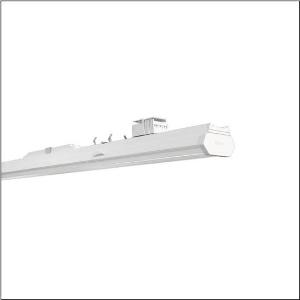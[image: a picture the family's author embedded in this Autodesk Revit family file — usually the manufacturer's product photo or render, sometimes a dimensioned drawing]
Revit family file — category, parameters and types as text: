
# Revit family: licross_r__11_protected_mo_51td12dn495g3c_9d50
name_source: partatom
category: Lighting Fixtures
units: mm (PartAtom-declared; Revit-internal decimal feet)

## family parameters
Cut with Voids When Loaded = No
Host = Face
Light Source = No
Part Type = Normal
Room Calculation Point = No
Round Connector Dimension = Use Diameter
Shared = No

## types (1)
- --- (1 x LED, 980 lm, 6.8 W, 4000K)
    Apparent Load = 7 VA
    CIE Flux Codes = 73 92 98 99 100
    Color Rendering = 80
    Color Temperature = 4000K
    Default Elevation = 1800 mm
    Description = Licross® 11 Protected MO, luminaire insert, of sheet steel, galvanised, coil coated, white, length: 1.500mm, width: 90mm, height: 101mm, LED rated luminous flux: 9.980lm, light colour: 840, control gear: DALI 2 (for two DALI lines), with plug, 6-pole, with phase selection, for trunking rail, 14-core, mains connection: 220..240V, AC, 50/60Hz, rated input power: 61W, for trunking rail, 14-core, halogen-free wiring, for emergency light function, converter,control gear: single battery element, battery: LiFePO4, 9Ah, primary light control with lens, of plastic, primary optical cover: cover, of PMMA, light emission: direct distribution, primary light characteristic: symmetric, protection rating (complete): IP54, insulation class (complete): insulation class I (protective earthing), certification: CE, UKCA, protection symbol: D if used in an environment with non-conductive dust loads with corresponding accessories, impact resistance: IK06, permissible ambient temperature for indoor applications: +5..+35°C, standard: EN 60598-2-22, LABS conformity tested according to VDMA 24364:2018-05, reducing of maximum allowable ambient temperature of 5°C with ceiling mounting, corresponds to IFS (International Featured Standards) requirements for safety and quality in the food industry, packaging unit: 1 piece
    Height = 92 mm
    Lamp = 1 x LED
    Lamp Light Flux = 980 lm
    Lamp Power = 6.8 W
    Lamp count = 1
    Length = 1500 mm
    Luminous efficacy = 144 lm/W
    Manufacturer = Siteco
    ModVariant = No
    Model = 51TD12DN495G3C
    Mounting Place = Ceiling
    Mounting Type = Pendant
    Number of Poles = 1
    OnlyDefault = Yes
    Power Factor = 1
    Product Name = Licross® 11 Protected MO
    Product group = luminaire insert
    ProductGroupID = 901
    Protection Class = Protection class I
    Protection Degree = IP 54
    RLX_Detail_Level = 1
    RLX_Emergency_Light_Flux = 0 lm
    RLX_Emergency_Type = 0
    RLX_Emergency_Type_DB = No
    RlxData = <blob elided: 24665 chars, md5=c544489d>
    Socket = socket
    Standby Power = 0 W
    System Light Flux = 980 lm
    System Power = 7 W
    Type Comments = : emergency light operation: 3 h
    Type Image = l_1256145.jpg
    URL = http://relux.com
    VarID = @adj_059445
    Voltage = 0 V
    Weight = 0.00 kg
    Width = 88 mm

## geometry (parser evidence)
native form markers: Blend x4, Sweep x10
no freeform markers — native parametric forms only
